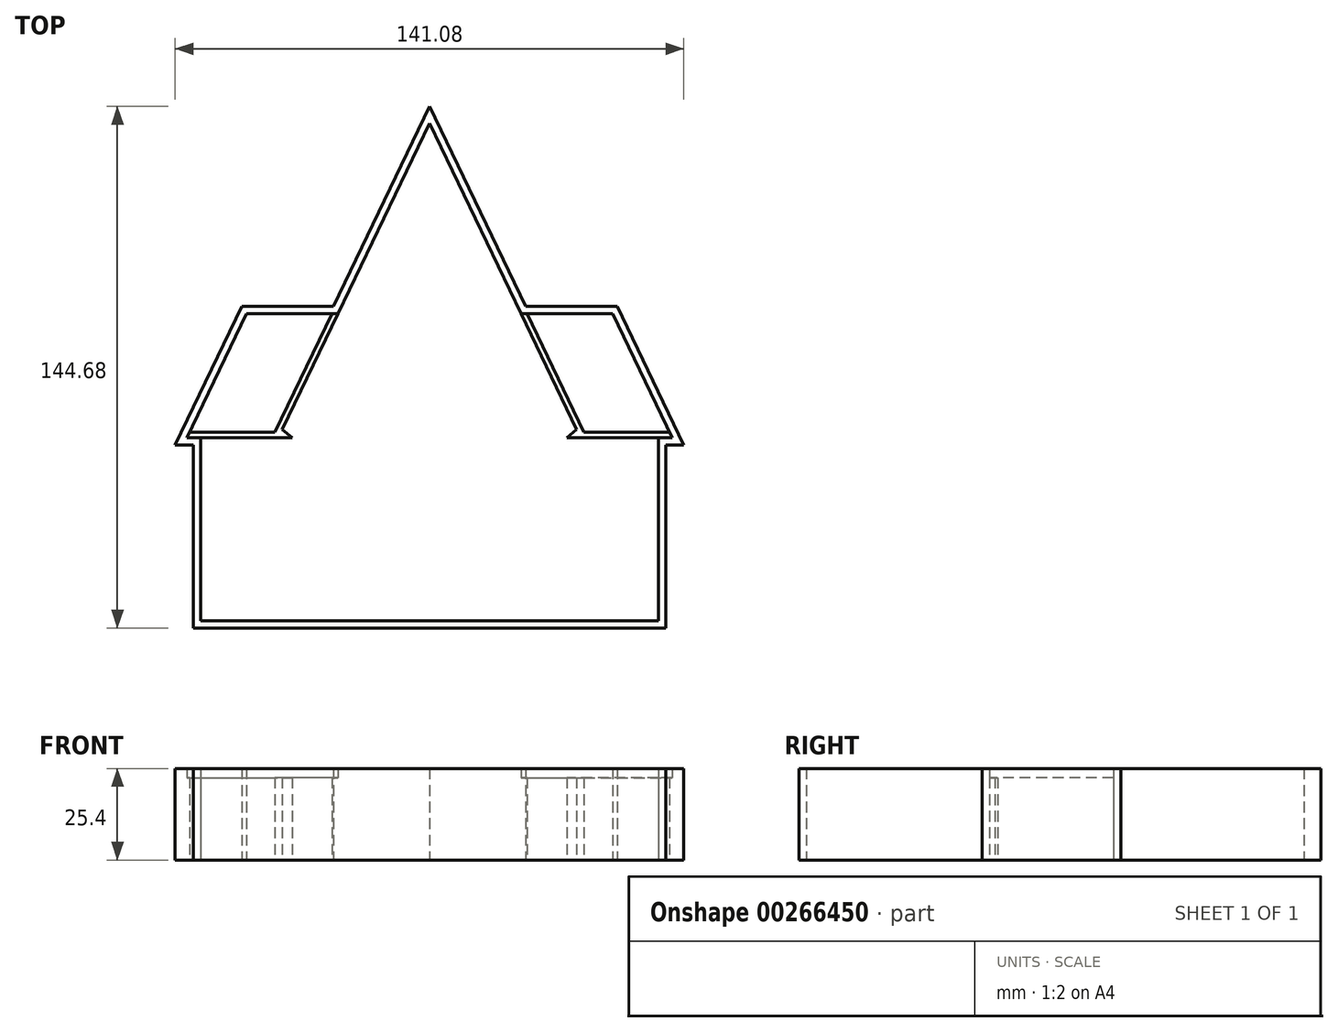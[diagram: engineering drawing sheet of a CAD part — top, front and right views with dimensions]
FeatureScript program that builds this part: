
annotation { "Feature Type Name" : "Feature", "Feature Type Description" : "" }
export const myFeature = defineFeature(function(context is Context, id is Id, definition is map)
    precondition{}
    {
        {
            var Q0;
            Q0=qCreatedBy(makeId("Top.planeOp"),FACE);
            var sketch = newSketch(context, id + "F0", { "sketchPlane" : qUnion([Q0])});
            skLineSegment(sketch, "E0", {"start": v(-58.74, -50.8) * mm, "end": v(68.26, -50.8) * mm});
            skLineSegment(sketch, "E1", {"start": v(-58.74, -50.8) * mm, "end": v(-58.74, 0) * mm});
            skLineSegment(sketch, "E2", {"start": v(68.26, -50.8) * mm, "end": v(68.26, 0) * mm});
            skLineSegment(sketch, "E3", {"start": v(-61.82, 1.52) * mm, "end": v(-46.04, 34.34) * mm});
            skLineSegment(sketch, "E4", {"start": v(-46.04, 34.34) * mm, "end": v(-22.33, 34.34) * mm});
            skLineSegment(sketch, "E5", {"start": v(71.34, 1.52) * mm, "end": v(55.56, 34.34) * mm});
            skLineSegment(sketch, "E6", {"start": v(55.56, 34.34) * mm, "end": v(30.16, 34.34) * mm});
            skLineSegment(sketch, "E7", {"start": v(-20.64, 34.34) * mm, "end": v(-36.05, 2.29) * mm});
            skLineSegment(sketch, "E8", {"start": v(30.16, 34.34) * mm, "end": v(45.57, 2.29) * mm});
            skLineSegment(sketch, "E9", {"start": v(68.26, 0) * mm, "end": v(42.86, 0) * mm});
            skLineSegment(sketch, "E10", {"start": v(42.86, 0) * mm, "end": v(45.57, 2.29) * mm});
            skLineSegment(sketch, "E11", {"start": v(-58.74, 0) * mm, "end": v(-33.34, 0) * mm});
            skLineSegment(sketch, "E12", {"start": v(-33.34, 0) * mm, "end": v(-36.05, 2.29) * mm});
            skLineSegment(sketch, "E13", {"start": v(30.16, 34.34) * mm, "end": v(4.76, 87.16) * mm});
            skLineSegment(sketch, "E14", {"start": v(4.76, 87.16) * mm, "end": v(-20.64, 34.34) * mm});
            skLineSegment(sketch, "E15", {"start": v(4.76, 60.75) * mm, "end": v(-5.15, 40.15) * mm});
            skLineSegment(sketch, "E16", {"start": v(4.76, 60.75) * mm, "end": v(14.66, 40.15) * mm});
            skLineSegment(sketch, "E17", {"start": v(14.66, 40.15) * mm, "end": v(14.66, 14.75) * mm});
            skLineSegment(sketch, "E18", {"start": v(-5.15, 40.15) * mm, "end": v(-5.15, 14.75) * mm});
            skLineSegment(sketch, "E19", {"start": v(-5.15, 14.75) * mm, "end": v(14.66, 14.75) * mm});
            skLineSegment(sketch, "E20", {"start": v(9.71, 14.75) * mm, "end": v(9.71, 50.45) * mm});
            skLineSegment(sketch, "E21", {"start": v(-0.2, 50.45) * mm, "end": v(-0.2, 14.75) * mm});
            skLineSegment(sketch, "E22", {"start": v(14.66, 27.45) * mm, "end": v(-5.15, 27.45) * mm});
            skLineSegment(sketch, "E23", {"start": v(14.66, 40.15) * mm, "end": v(-5.15, 40.15) * mm});
            skLineSegment(sketch, "E24.0", {"start": v(-58.74, 1.52) * mm, "end": v(-38.11, 1.52) * mm});
            skLineSegment(sketch, "E24.1", {"start": v(-22.33, 34.34) * mm, "end": v(-38.11, 1.52) * mm});
            skLineSegment(sketch, "E25", {"start": v(-58.74, 1.52) * mm, "end": v(-61.82, 1.52) * mm});
            skLineSegment(sketch, "E26.0", {"start": v(68.26, 1.52) * mm, "end": v(47.63, 1.52) * mm});
            skLineSegment(sketch, "E26.1", {"start": v(31.85, 34.34) * mm, "end": v(47.63, 1.52) * mm});
            skLineSegment(sketch, "E27", {"start": v(68.26, 1.52) * mm, "end": v(71.34, 1.52) * mm});
            skLineSegment(sketch, "E28", {"start": v(-22.33, 34.34) * mm, "end": v(-20.64, 34.34) * mm});
            skLineSegment(sketch, "E29", {"start": v(-61.82, 1.52) * mm, "end": v(-62.55, 0) * mm});
            skLineSegment(sketch, "E30", {"start": v(-62.55, 0) * mm, "end": v(-58.74, 0) * mm});
            skLineSegment(sketch, "E31", {"start": v(71.34, 1.52) * mm, "end": v(72.07, 0) * mm});
            skLineSegment(sketch, "E32", {"start": v(68.26, 0) * mm, "end": v(72.07, 0) * mm});
            skLineSegment(sketch, "E33.0", {"start": v(31.44, 36.37) * mm, "end": v(4.76, 91.85) * mm});
            skLineSegment(sketch, "E33.1", {"start": v(56.84, 36.37) * mm, "end": v(31.44, 36.37) * mm});
            skLineSegment(sketch, "E33.2", {"start": v(72.68, 3.42) * mm, "end": v(56.84, 36.37) * mm});
            skLineSegment(sketch, "E33.3", {"start": v(-63.16, 3.42) * mm, "end": v(-65.78, -2.03) * mm});
            skLineSegment(sketch, "E33.4", {"start": v(-63.16, 3.42) * mm, "end": v(-47.32, 36.37) * mm});
            skLineSegment(sketch, "E33.5", {"start": v(-47.32, 36.37) * mm, "end": v(-23.46, 36.37) * mm});
            skLineSegment(sketch, "E33.6", {"start": v(-23.46, 36.37) * mm, "end": v(-21.92, 36.37) * mm});
            skLineSegment(sketch, "E33.7", {"start": v(-65.78, -2.03) * mm, "end": v(-60.77, -2.03) * mm});
            skLineSegment(sketch, "E33.8", {"start": v(-60.77, -52.83) * mm, "end": v(-60.77, -2.03) * mm});
            skLineSegment(sketch, "E33.9", {"start": v(-60.77, -52.83) * mm, "end": v(70.3, -52.83) * mm});
            skLineSegment(sketch, "E33.10", {"start": v(4.76, 91.85) * mm, "end": v(-21.92, 36.37) * mm});
            skLineSegment(sketch, "E33.11", {"start": v(70.3, -52.83) * mm, "end": v(70.3, -2.03) * mm});
            skLineSegment(sketch, "E33.12", {"start": v(70.3, -2.03) * mm, "end": v(75.3, -2.03) * mm});
            skLineSegment(sketch, "E33.13", {"start": v(72.68, 3.42) * mm, "end": v(75.3, -2.03) * mm});
            skSolve(sketch);
        }
        {
            var Q0;
            Q0=makeQuery(id+"F0.imprint","IMPRINT",FACE,{"disambiguationData":[TD([[makeQuery(id+"F0.imprint","IMPRINT",EDGE,{"derivedFrom":sQuery(id+"F0.wireOp",EDGE,"E0")}),-1.0]])]});
            extrude(context, id + "F1", {"entities" : qUnion([Q0]), "depth" : 25.4 * mm});
        }
        {
            var Q0;
            Q0=makeQuery(id+"F0.imprint","IMPRINT",FACE,{"disambiguationData":[TD([[makeQuery(id+"F0.imprint","IMPRINT",EDGE,{"derivedFrom":sQuery(id+"F0.wireOp",EDGE,"E7")}),-1.0]])]});
            var Q1;
            {var subQ1=sQuery(id+"F0.wireOp",EDGE,"E8");Q1=makeQuery(id+"F0.imprint","IMPRINT",FACE,{"disambiguationData":[TD([[makeQuery(id+"F0.imprint","IMPRINT",EDGE,{"derivedFrom":subQ1}),1.0]])]});}
            extrude(context, id + "F2", {"entities" : qUnion([Q0, Q1]), "operationType" : NewBodyOperationType.ADD, "depth" : 22.86 * mm});
        }
    });
